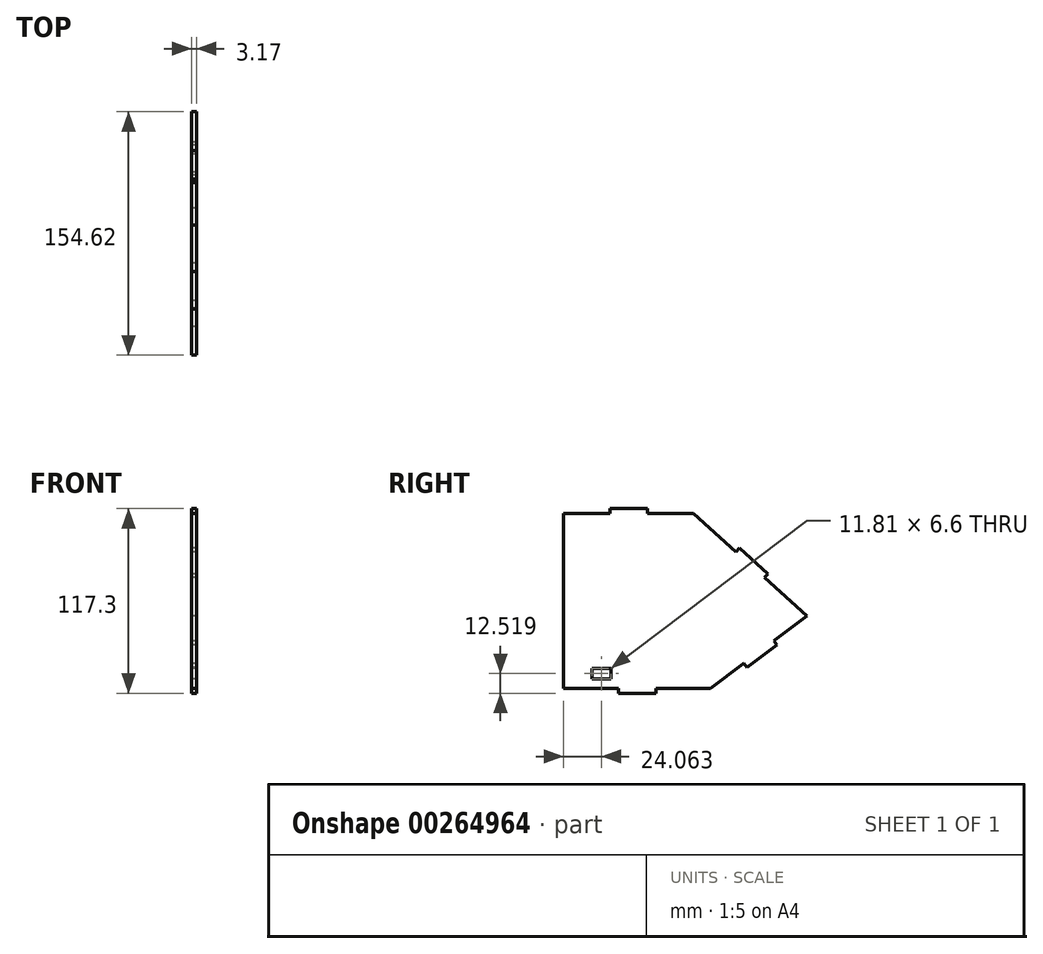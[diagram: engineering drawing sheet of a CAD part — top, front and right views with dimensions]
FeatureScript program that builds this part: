
annotation { "Feature Type Name" : "Feature", "Feature Type Description" : "" }
export const myFeature = defineFeature(function(context is Context, id is Id, definition is map)
    precondition{}
    {
        {
            var Q0;
            Q0=qCreatedBy(makeId("Right.planeOp"),FACE);
            var sketch = newSketch(context, id + "F0", { "sketchPlane" : qUnion([Q0])});
            skLineSegment(sketch, "E0", {"start": v(33.96, 45.94) * mm, "end": v(5.6, 45.94) * mm});
            skPoint(sketch, "E1.MirrorCS.end.orphan", {"position": v(-48.2, -63.5) * mm});
            skLineSegment(sketch, "E2", {"start": v(-48.65, -22.24) * mm, "end": v(-48.65, -65.02) * mm});
            skPoint(sketch, "E3.MirrorCS.start.orphan", {"position": v(-48.2, -63.34) * mm});
            skLineSegment(sketch, "E4", {"start": v(-48.65, -65.02) * mm, "end": v(-14.64, -65.02) * mm});
            skLineSegment(sketch, "E5", {"start": v(44.77, -65.02) * mm, "end": v(65.23, -49.6) * mm});
            skPoint(sketch, "E6.end.orphan", {"position": v(33.96, 48.11) * mm});
            skPoint(sketch, "E7", {"position": v(24.2, -9.62) * mm});
            skPoint(sketch, "E8", {"position": v(85.6, -0.58) * mm});
            skPoint(sketch, "E9.end.orphan", {"position": v(85.6, -9.62) * mm});
            skLineSegment(sketch, "E10", {"start": v(-30.5, -52.37) * mm, "end": v(-30.5, -58.97) * mm});
            skLineSegment(sketch, "E11", {"start": v(-30.5, -52.37) * mm, "end": v(-18.68, -52.37) * mm});
            skLineSegment(sketch, "E12", {"start": v(-18.68, -52.37) * mm, "end": v(-18.68, -58.97) * mm});
            skLineSegment(sketch, "E13", {"start": v(-18.68, -58.97) * mm, "end": v(-30.5, -58.97) * mm});
            skLineSegment(sketch, "E14", {"start": v(44.77, -65.02) * mm, "end": v(11.01, -65.02) * mm});
            skLineSegment(sketch, "E15", {"start": v(-1.94, -68.2) * mm, "end": v(9.96, -68.2) * mm});
            skLineSegment(sketch, "E16.MirrorCS", {"start": v(-1.94, -68.2) * mm, "end": v(-13.85, -68.2) * mm});
            skPoint(sketch, "E17.orphan", {"position": v(-1.94, -65.02) * mm});
            skLineSegment(sketch, "E18.trimOffspring", {"start": v(11.01, -65.02) * mm, "end": v(44.77, -65.02) * mm});
            skLineSegment(sketch, "E19", {"start": v(-7.35, 49.11) * mm, "end": v(4.56, 49.11) * mm});
            skLineSegment(sketch, "E20.MirrorCS", {"start": v(-7.35, 49.11) * mm, "end": v(-19.25, 49.11) * mm});
            skLineSegment(sketch, "E21.trimOffspring", {"start": v(-20.05, 45.94) * mm, "end": v(-48.65, 45.94) * mm});
            skPoint(sketch, "E22.orphan", {"position": v(-7.35, 45.94) * mm});
            skLineSegment(sketch, "E23", {"start": v(-48.65, 45.94) * mm, "end": v(-48.65, 3.16) * mm});
            skPoint(sketch, "E24", {"position": v(-51.83, -9.54) * mm});
            skPoint(sketch, "E25.orphan", {"position": v(-52.38, -9.54) * mm});
            skPoint(sketch, "E26.orphan", {"position": v(-48.65, -9.54) * mm});
            skLineSegment(sketch, "E27", {"start": v(105.97, -18.9) * mm, "end": v(79.59, 4.85) * mm});
            skLineSegment(sketch, "E28", {"start": v(72.09, 15.88) * mm, "end": v(81.12, 7.74) * mm});
            skLineSegment(sketch, "E29.MirrorCS", {"start": v(72.09, 15.88) * mm, "end": v(63.05, 24.02) * mm});
            skLineSegment(sketch, "E30.trimOffspring", {"start": v(60.52, 22.02) * mm, "end": v(33.96, 45.94) * mm});
            skPoint(sketch, "E31.orphan", {"position": v(69.96, 13.52) * mm});
            skLineSegment(sketch, "E32", {"start": v(105.97, -18.9) * mm, "end": v(85.71, -34.16) * mm});
            skLineSegment(sketch, "E33", {"start": v(77.28, -44.5) * mm, "end": v(86.79, -37.33) * mm});
            skLineSegment(sketch, "E34.MirrorCS", {"start": v(77.28, -44.5) * mm, "end": v(67.77, -51.66) * mm});
            skPoint(sketch, "E35.orphan", {"position": v(75.37, -41.96) * mm});
            skLineSegment(sketch, "E36", {"start": v(-48.65, -22.24) * mm, "end": v(-48.65, 3.16) * mm});
            skLineSegment(sketch, "E37", {"start": v(-20.05, 45.94) * mm, "end": v(-19.25, 45.94) * mm});
            skLineSegment(sketch, "E38", {"start": v(-19.25, 45.94) * mm, "end": v(-19.25, 49.11) * mm});
            skLineSegment(sketch, "E39.MirrorCS", {"start": v(4.56, 45.94) * mm, "end": v(4.56, 49.11) * mm});
            skLineSegment(sketch, "E40.MirrorCS", {"start": v(5.35, 45.94) * mm, "end": v(4.56, 45.94) * mm});
            skLineSegment(sketch, "E41", {"start": v(5.35, 45.94) * mm, "end": v(5.6, 45.94) * mm});
            skLineSegment(sketch, "E42", {"start": v(-14.64, -65.02) * mm, "end": v(-13.85, -65.02) * mm});
            skLineSegment(sketch, "E43", {"start": v(-13.85, -65.02) * mm, "end": v(-13.85, -68.2) * mm});
            skLineSegment(sketch, "E44.MirrorCS", {"start": v(9.96, -65.02) * mm, "end": v(9.96, -68.2) * mm});
            skLineSegment(sketch, "E45.MirrorCS", {"start": v(10.76, -65.02) * mm, "end": v(9.96, -65.02) * mm});
            skLineSegment(sketch, "E46", {"start": v(10.76, -65.02) * mm, "end": v(11.01, -65.02) * mm});
            skLineSegment(sketch, "E47", {"start": v(67.77, -51.66) * mm, "end": v(65.86, -49.12) * mm});
            skLineSegment(sketch, "E48", {"start": v(65.86, -49.12) * mm, "end": v(65.23, -49.6) * mm});
            skLineSegment(sketch, "E49.MirrorCS", {"start": v(86.79, -37.33) * mm, "end": v(84.88, -34.8) * mm});
            skLineSegment(sketch, "E50.MirrorCS", {"start": v(84.88, -34.8) * mm, "end": v(85.51, -34.32) * mm});
            skLineSegment(sketch, "E51", {"start": v(85.71, -34.16) * mm, "end": v(85.51, -34.32) * mm});
            skLineSegment(sketch, "E52", {"start": v(79.59, 4.85) * mm, "end": v(79, 5.38) * mm});
            skLineSegment(sketch, "E53", {"start": v(79, 5.38) * mm, "end": v(81.12, 7.74) * mm});
            skLineSegment(sketch, "E54", {"start": v(72.09, 15.88) * mm, "end": v(70.86, 14.52) * mm});
            skLineSegment(sketch, "E55.MirrorCS", {"start": v(60.93, 21.66) * mm, "end": v(63.05, 24.02) * mm});
            skLineSegment(sketch, "E56.MirrorCS", {"start": v(60.34, 22.19) * mm, "end": v(60.93, 21.66) * mm});
            skSolve(sketch);
        }
        {
            var Q0;
            Q0=makeQuery(id+"F0.imprint","IMPRINT",FACE,{"disambiguationData":[TD([[makeQuery(id+"F0.imprint","IMPRINT",EDGE,{"derivedFrom":sQuery(id+"F0.wireOp",EDGE,"E2")}),1.0]])]});
            extrude(context, id + "F1", {"entities" : qUnion([Q0]), "depth" : 3.17 * mm, "offsetDistance" : 25.4 * mm});
        }
    });
